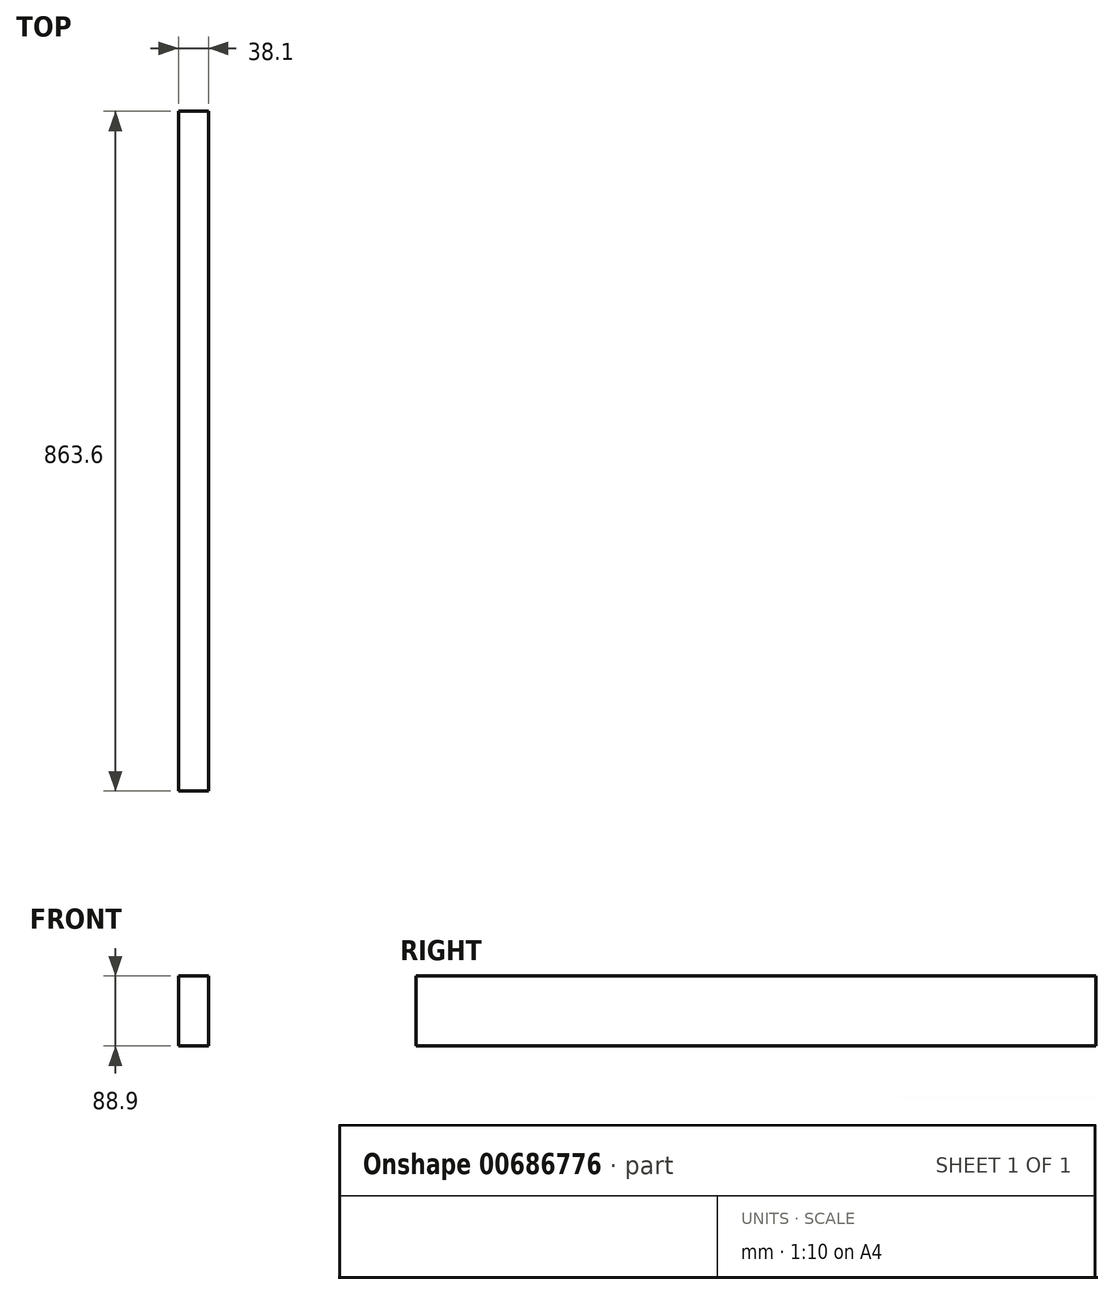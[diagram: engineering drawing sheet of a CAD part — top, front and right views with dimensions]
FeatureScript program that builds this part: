
annotation { "Feature Type Name" : "Feature", "Feature Type Description" : "" }
export const myFeature = defineFeature(function(context is Context, id is Id, definition is map)
    precondition{}
    {
        {
            var Q0;
            Q0=qCreatedBy(makeId("Front.planeOp"),FACE);
            var sketch = newSketch(context, id + "F0", { "sketchPlane" : qUnion([Q0])});
            skLineSegment(sketch, "E0.bottom", {"start": v(19.05, -44.45) * mm, "end": v(-19.05, -44.45) * mm});
            skLineSegment(sketch, "E0.top", {"start": v(19.05, 44.45) * mm, "end": v(-19.05, 44.45) * mm});
            skLineSegment(sketch, "E0.left", {"start": v(19.05, -44.45) * mm, "end": v(19.05, 44.45) * mm});
            skLineSegment(sketch, "E0.right", {"start": v(-19.05, -44.45) * mm, "end": v(-19.05, 44.45) * mm});
            skPoint(sketch, "E0.middle", {"position": v(0, 0) * mm});
            skSolve(sketch);
        }
        {
            var Q0;
            Q0 = qSketchRegion(id + "F0", true);
            extrude(context, id + "F1", {"entities" : qUnion([Q0]), "depth" : 431.8 * mm, "offsetDistance" : 25.4 * mm, "hasSecondDirection" : true, "secondDirectionOppositeDirection" : true, "secondDirectionDepth" : 431.8 * mm});
        }
    });
